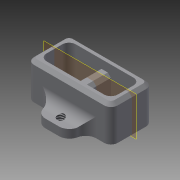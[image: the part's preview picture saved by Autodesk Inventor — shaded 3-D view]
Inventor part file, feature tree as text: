
AUTODESK INVENTOR PART (.ipt)
format: ipt  version: 2015 (Build 190159000, 159)  size: 215,552 bytes
history: native  units: in
note: dims shown in document units (in); Inventor stores cm internally (conversion verified against a paired STEP export)
features: sketch x6, extrude x5, fillet x3, chamfer x3, plane x1, mirror x1, hole x1
ambient origin geometry x8: Origin, YZ Plane, XZ Plane, XY Plane, X Axis, Y Axis, Z Axis, Center Point
bodies: Solid1 (feature_tree)
feature tree (20):
  extrude  "Extrusion1"  Depth=1.0in
  extrude  "Extrusion2"  Depth=0.85in
  extrude  "Extrusion3"  Depth=0.1in TaperAngle=0.0deg
  extrude  "Extrusion4"  Depth=0.35in
  extrude  "Extrusion5"  Depth=0.35in
  plane  "Work Plane1"
  mirror  "Mirror1"
  fillet  "Fillet1"  Radius=0.25in
  fillet  "Fillet2"  Radius=0.1in
  fillet  "Fillet3"  Radius=0.25in
  chamfer  "Chamfer1"  Distance=0.25in
  chamfer  "Chamfer2"  Distance=0.4in
  chamfer  "Chamfer3"  Distance=0.2in
  hole  "Hole1"  [1 undecoded]
  sketch  "Sketch1"  dims[d0=0.5in d1=1.0in]
  sketch  "Sketch2"  dims[d2=0.375in d3=0.05in d4=0.0in d5=0.0in d6=0.85in]
  sketch  "Sketch3"  dims[d7=0.35in d8=0.1in d9=0.0in]
  sketch  "Sketch4"  dims[d10=0.35in d11=0.35in]
  sketch  "Sketch5"  dims[d12=0.35in d13=0.35in d14=0.25in d15=0.0in d16=0.1in d17=0.25in]
  sketch  "Sketch7"  dims[d18=0.1in d19=0.25in d20=0.0in d21=0.4in d22=0.2in d23=0.1in d24=0.0in d25=0.125in d26=0.125in d27=0.08in d32=0.0375in d33=0.125in d34=45.0deg d35=0.0375in d36=0.125in d37=45.0deg d38=0.0375in d39=0.125in d40=45.0deg d41=0.35in d42=0.085in d43=0.224in d44=0.119in d45=0.25in d46=0.5635in d47=0.4in d48=0.8108in]
note: 1 required parameter value undecoded (feature->parameter linkage not recoverable at this tier; creation-order binding heuristic only, values carry confidence <= 0.55)
